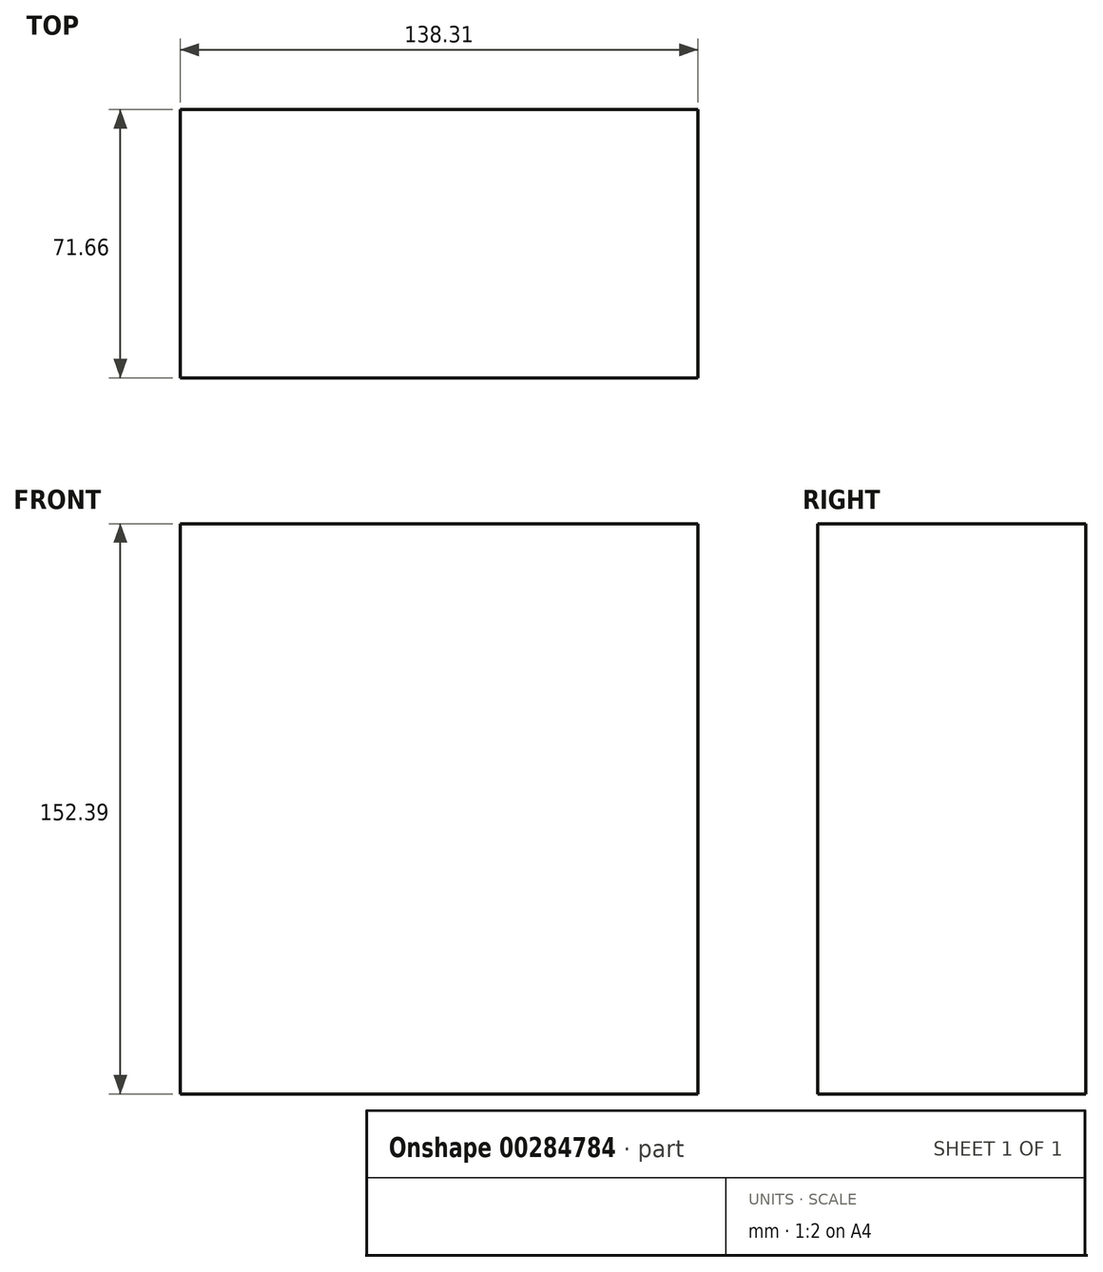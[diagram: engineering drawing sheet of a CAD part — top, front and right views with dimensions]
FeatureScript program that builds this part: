
annotation { "Feature Type Name" : "Feature", "Feature Type Description" : "" }
export const myFeature = defineFeature(function(context is Context, id is Id, definition is map)
    precondition{}
    {
        {
            var Q0;
            Q0=qCreatedBy(makeId("Front.planeOp"),FACE);
            var sketch = newSketch(context, id + "F0", { "sketchPlane" : qUnion([Q0])});
            skLineSegment(sketch, "E0.bottom", {"start": v(68.06, -79.21) * mm, "end": v(-70.25, -79.21) * mm});
            skLineSegment(sketch, "E0.top", {"start": v(68.06, 73.18) * mm, "end": v(-70.25, 73.18) * mm});
            skLineSegment(sketch, "E0.left", {"start": v(68.06, -79.21) * mm, "end": v(68.06, 73.18) * mm});
            skLineSegment(sketch, "E0.right", {"start": v(-70.25, -79.21) * mm, "end": v(-70.25, 73.18) * mm});
            skSolve(sketch);
        }
        {
            var Q0;
            Q0=makeQuery(id+"F0.imprint","IMPRINT",FACE,{"disambiguationData":[TD([[makeQuery(id+"F0.imprint","IMPRINT",EDGE,{"derivedFrom":sQuery(id+"F0.wireOp",EDGE,"E0.bottom")}),-1.0]])]});
            extrude(context, id + "F1", {"entities" : qUnion([Q0]), "depth" : 71.66 * mm});
        }
    });
